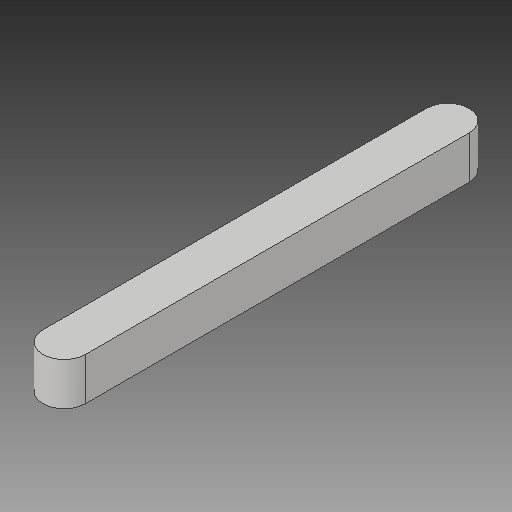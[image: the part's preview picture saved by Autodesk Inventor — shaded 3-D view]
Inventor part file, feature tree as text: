
AUTODESK INVENTOR PART (.ipt)
format: ipt  version: 2018 (Build 220112000, 112)  size: 79,360 bytes
history: native  units: in
note: dims shown in document units (in); Inventor stores cm internally (conversion verified against a paired STEP export)
features: fillet x1
ambient origin geometry x8: Origin, YZ Plane, XZ Plane, XY Plane, X Axis, Y Axis, Z Axis, Center Point
bodies: Solid1 (feature_tree)
feature tree (1):
  fillet  "Fillet1"  [1 undecoded]
note: 1 required parameter value undecoded (feature->parameter linkage not recoverable at this tier; creation-order binding heuristic only, values carry confidence <= 0.55)
